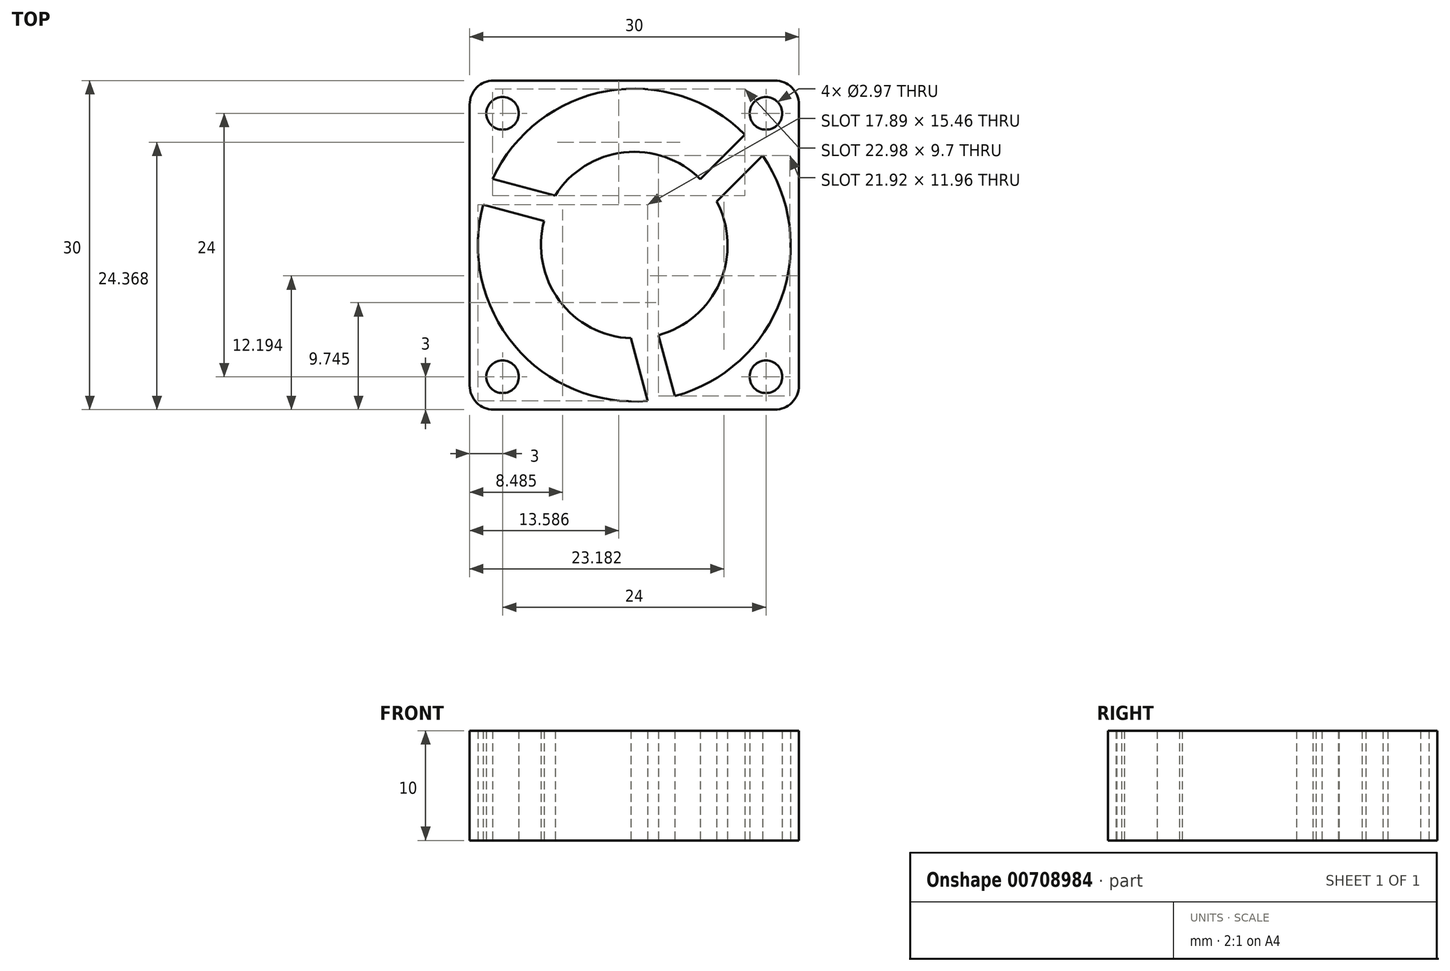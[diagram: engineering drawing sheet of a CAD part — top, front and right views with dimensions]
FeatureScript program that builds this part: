
annotation { "Feature Type Name" : "Feature", "Feature Type Description" : "" }
export const myFeature = defineFeature(function(context is Context, id is Id, definition is map)
    precondition{}
    {
        {
            var Q0;
            Q0=qCreatedBy(makeId("Top.planeOp"),FACE);
            var sketch = newSketch(context, id + "F0", { "sketchPlane" : qUnion([Q0])});
            skLineSegment(sketch, "E0.bottom", {"start": v(12.8, -15) * mm, "end": v(-12.8, -15) * mm});
            skLineSegment(sketch, "E0.top", {"start": v(12.8, 15) * mm, "end": v(-12.8, 15) * mm});
            skLineSegment(sketch, "E0.left", {"start": v(15, -12.8) * mm, "end": v(15, 12.8) * mm});
            skLineSegment(sketch, "E0.right", {"start": v(-15, -12.8) * mm, "end": v(-15, 12.8) * mm});
            skPoint(sketch, "E0.middle", {"position": v(0, 0) * mm});
            skCircle(sketch, "E1", {"center": v(0, 0) * mm, "radius": 14.25 * mm});
            skCircle(sketch, "E2", {"center": v(-12, 12) * mm, "radius": 1.49 * mm});
            skCircle(sketch, "E3", {"center": v(12, 12) * mm, "radius": 1.49 * mm});
            skCircle(sketch, "E4", {"center": v(12, -12) * mm, "radius": 1.49 * mm});
            skCircle(sketch, "E5", {"center": v(-12, -12) * mm, "radius": 1.49 * mm});
            skLineSegment(sketch, "E6", {"start": v(-15, -15) * mm, "end": v(15, 15) * mm});
            skLineSegment(sketch, "E7", {"start": v(-15, 15) * mm, "end": v(15, -15) * mm});
            skPoint(sketch, "E8.visualSharp", {"position": v(-15, 15) * mm});
            skArc(sketch, "E8.filletArc", {"start": v(-12.8, 15) * mm, "mid": v(-14.36, 14.36) * mm, "end": v(-15, 12.8) * mm});
            skPoint(sketch, "E9.visualSharp", {"position": v(15, 15) * mm});
            skArc(sketch, "E9.filletArc", {"start": v(15, 12.8) * mm, "mid": v(14.36, 14.36) * mm, "end": v(12.8, 15) * mm});
            skPoint(sketch, "E10.visualSharp", {"position": v(15, -15) * mm});
            skArc(sketch, "E10.filletArc", {"start": v(12.8, -15) * mm, "mid": v(14.36, -14.36) * mm, "end": v(15, -12.8) * mm});
            skPoint(sketch, "E11.visualSharp", {"position": v(-15, -15) * mm});
            skArc(sketch, "E11.filletArc", {"start": v(-15, -12.8) * mm, "mid": v(-14.36, -14.36) * mm, "end": v(-12.8, -15) * mm});
            skLineSegment(sketch, "E12", {"start": v(0, 0) * mm, "end": v(-13.76, 3.69) * mm});
            skLineSegment(sketch, "E13", {"start": v(0, 0) * mm, "end": v(3.69, -13.76) * mm});
            skCircle(sketch, "E14", {"center": v(0, 0) * mm, "radius": 8.5 * mm});
            skLineSegment(sketch, "E15", {"start": v(-12.9, 6.05) * mm, "end": v(-7.2, 4.52) * mm});
            skLineSegment(sketch, "E16", {"start": v(7.51, 3.98) * mm, "end": v(11.69, 8.15) * mm});
            skLineSegment(sketch, "E17", {"start": v(-0.31, -8.5) * mm, "end": v(1.22, -14.2) * mm});
            skSolve(sketch);
        }
        {
            var Q0;
            {var subQ4=sQuery(id+"F0.wireOp",EDGE,"E0.right");Q0=makeQuery(id+"F0.imprint","IMPRINT",FACE,{"disambiguationData":[TD([[makeQuery(id+"F0.imprint","IMPRINT",EDGE,{"derivedFrom":subQ4}),-1.0]])]});}
            var Q1;
            {var subQ9=sQuery(id+"F0.wireOp",EDGE,"E0.bottom");Q1=makeQuery(id+"F0.imprint","IMPRINT",FACE,{"disambiguationData":[TD([[makeQuery(id+"F0.imprint","IMPRINT",EDGE,{"derivedFrom":subQ9}),-1.0]])]});}
            var Q2;
            {var subQ4=sQuery(id+"F0.wireOp",EDGE,"E0.left");Q2=makeQuery(id+"F0.imprint","IMPRINT",FACE,{"disambiguationData":[TD([[makeQuery(id+"F0.imprint","IMPRINT",EDGE,{"derivedFrom":subQ4}),1.0]])]});}
            var Q3;
            {var subQ7=sQuery(id+"F0.wireOp",EDGE,"E0.top");Q3=makeQuery(id+"F0.imprint","IMPRINT",FACE,{"disambiguationData":[TD([[makeQuery(id+"F0.imprint","IMPRINT",EDGE,{"derivedFrom":subQ7}),1.0]])]});}
            var Q4;
            {var subQ3=sQuery(id+"F0.wireOp",EDGE,"E15");Q4=makeQuery(id+"F0.imprint","IMPRINT",FACE,{"disambiguationData":[TD([[makeQuery(id+"F0.imprint","IMPRINT",EDGE,{"derivedFrom":subQ3}),-1.0]])]});}
            var Q5;
            {var subQ3=sQuery(id+"F0.wireOp",EDGE,"E14");var subQ5=makeQuery(id+"F0.imprint","INTERSECT",VERTEX,{"derivedFrom":[subQ3,sQuery(id+"F0.wireOp",EDGE,"E15")]});Q5=makeQuery(id+"F0.imprint","IMPRINT",FACE,{"disambiguationData":[TD([[makeQuery(id+"F0.imprint","IMPRINT",EDGE,{"disambiguationData":[TD([[subQ5,1.0]])],"derivedFrom":subQ3}),1.0]])]});}
            var Q6;
            {var subQ1=sQuery(id+"F0.wireOp",EDGE,"E6");var subQ3=sQuery(id+"F0.wireOp",EDGE,"E14");var subQ4=makeQuery(id+"F0.imprint","INTERSECT",VERTEX,{"disambiguationData":[OD(1.0)],"derivedFrom":[subQ1,subQ3]});Q6=makeQuery(id+"F0.imprint","IMPRINT",FACE,{"disambiguationData":[TD([[makeQuery(id+"F0.imprint","IMPRINT",EDGE,{"disambiguationData":[TD([[subQ4,-1.0]])],"derivedFrom":subQ3}),1.0]])]});}
            var Q7;
            {var subQ3=sQuery(id+"F0.wireOp",EDGE,"E14");var subQ6=makeQuery(id+"F0.imprint","INTERSECT",VERTEX,{"derivedFrom":[subQ3,sQuery(id+"F0.wireOp",EDGE,"E16")]});Q7=makeQuery(id+"F0.imprint","IMPRINT",FACE,{"disambiguationData":[TD([[makeQuery(id+"F0.imprint","IMPRINT",EDGE,{"disambiguationData":[TD([[subQ6,-1.0]])],"derivedFrom":subQ3}),1.0]])]});}
            var Q8;
            {var subQ0=sQuery(id+"F0.wireOp",EDGE,"E16");Q8=makeQuery(id+"F0.imprint","IMPRINT",FACE,{"disambiguationData":[TD([[makeQuery(id+"F0.imprint","IMPRINT",EDGE,{"derivedFrom":subQ0}),1.0]])]});}
            var Q9;
            {var subQ1=sQuery(id+"F0.wireOp",EDGE,"E7");var subQ3=sQuery(id+"F0.wireOp",EDGE,"E14");var subQ4=makeQuery(id+"F0.imprint","INTERSECT",VERTEX,{"disambiguationData":[OD(1.0)],"derivedFrom":[subQ1,subQ3]});Q9=makeQuery(id+"F0.imprint","IMPRINT",FACE,{"disambiguationData":[TD([[makeQuery(id+"F0.imprint","IMPRINT",EDGE,{"disambiguationData":[TD([[subQ4,1.0]])],"derivedFrom":subQ3}),1.0]])]});}
            var Q10;
            {var subQ3=sQuery(id+"F0.wireOp",EDGE,"E14");var subQ6=makeQuery(id+"F0.imprint","INTERSECT",VERTEX,{"derivedFrom":[subQ3,sQuery(id+"F0.wireOp",EDGE,"E17")]});Q10=makeQuery(id+"F0.imprint","IMPRINT",FACE,{"disambiguationData":[TD([[makeQuery(id+"F0.imprint","IMPRINT",EDGE,{"disambiguationData":[TD([[subQ6,1.0]])],"derivedFrom":subQ3}),1.0]])]});}
            var Q11;
            {var subQ1=sQuery(id+"F0.wireOp",EDGE,"E6");var subQ3=sQuery(id+"F0.wireOp",EDGE,"E14");var subQ4=makeQuery(id+"F0.imprint","INTERSECT",VERTEX,{"disambiguationData":[OD(0.0)],"derivedFrom":[subQ1,subQ3]});Q11=makeQuery(id+"F0.imprint","IMPRINT",FACE,{"disambiguationData":[TD([[makeQuery(id+"F0.imprint","IMPRINT",EDGE,{"disambiguationData":[TD([[subQ4,1.0]])],"derivedFrom":subQ3}),1.0]])]});}
            var Q12;
            {var subQ3=sQuery(id+"F0.wireOp",EDGE,"E17");Q12=makeQuery(id+"F0.imprint","IMPRINT",FACE,{"disambiguationData":[TD([[makeQuery(id+"F0.imprint","IMPRINT",EDGE,{"derivedFrom":subQ3}),1.0]])]});}
            extrude(context, id + "F1", {"entities" : qUnion([Q0, Q1, Q2, Q3, Q4, Q5, Q6, Q7, Q8, Q9, Q10, Q11, Q12]), "depth" : 10 * mm, "offsetDistance" : 25 * mm});
        }
    });
